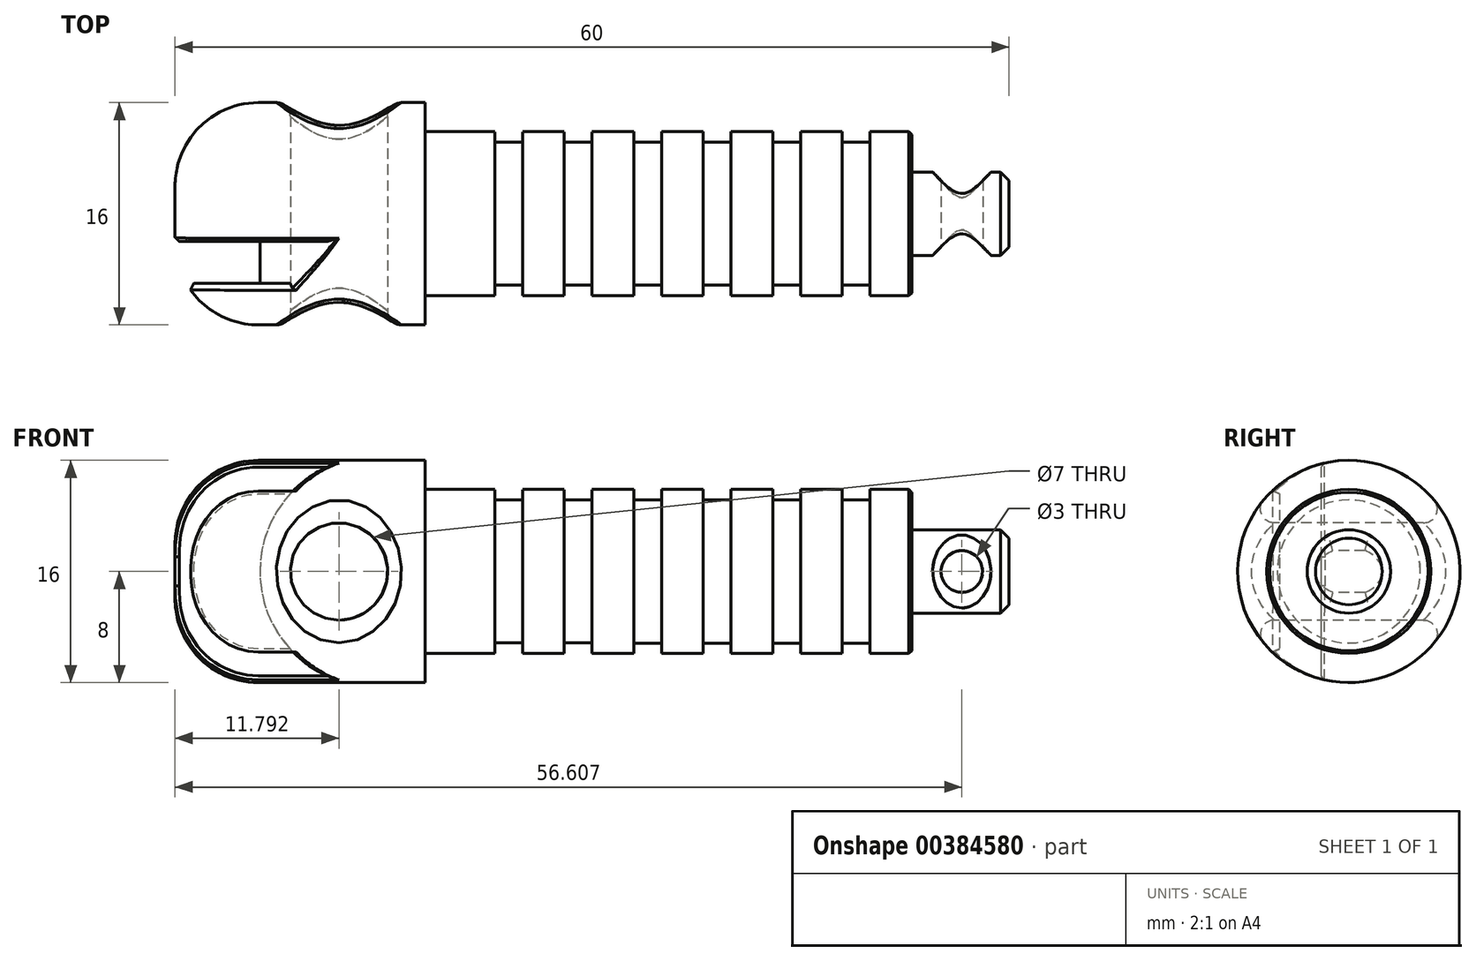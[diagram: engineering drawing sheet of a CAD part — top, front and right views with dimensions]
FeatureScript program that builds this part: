
annotation { "Feature Type Name" : "Feature", "Feature Type Description" : "" }
export const myFeature = defineFeature(function(context is Context, id is Id, definition is map)
    precondition{}
    {
        {
            var Q0;
            Q0=qCreatedBy(makeId("Right.planeOp"),FACE);
            var sketch = newSketch(context, id + "F0", { "sketchPlane" : qUnion([Q0])});
            skCircle(sketch, "E0", {"center": v(0, 0) * mm, "radius": 3 * mm});
            skSolve(sketch);
        }
        {
            var Q0;
            Q0=qSketchRegion(id+"F0",true);
            extrude(context, id + "F1", {"entities" : qUnion([Q0]), "depth" : 7 * mm});
        }
        {
            var Q0;
            Q0=makeQuery(id+"F1.opExtrude","CAP_FACE",FACE,{"disambiguationData":[OSD([sQuery(id+"F0.wireOp",EDGE,"E0")])],"isStart":true});
            var sketch = newSketch(context, id + "F2", { "sketchPlane" : qUnion([Q0])});
            skCircle(sketch, "E1", {"center": v(0, 0) * mm, "radius": 5.9 * mm});
            skSolve(sketch);
        }
        {
            var Q0;
            Q0=qSketchRegion(id+"F2",true);
            extrude(context, id + "F3", {"entities" : qUnion([Q0]), "operationType" : NewBodyOperationType.ADD, "depth" : 8 * mm});
        }
        {
            var Q0;
            Q0=makeQuery(id+"F3.opExtrude","CAP_FACE",FACE,{"disambiguationData":[OSD([sQuery(id+"F2.wireOp",EDGE,"E1")])],"isStart":false});
            var sketch = newSketch(context, id + "F4", { "sketchPlane" : qUnion([Q0])});
            skCircle(sketch, "E2", {"center": v(0, 0) * mm, "radius": 5.15 * mm});
            skSolve(sketch);
        }
        {
            var Q0;
            Q0=qSketchRegion(id+"F4",true);
            extrude(context, id + "F5", {"entities" : qUnion([Q0]), "operationType" : NewBodyOperationType.ADD, "depth" : 2 * mm});
        }
        {
            var Q0;
            Q0=makeQuery(id+"F5.opExtrude","CAP_FACE",FACE,{"disambiguationData":[OSD([sQuery(id+"F4.wireOp",EDGE,"E2")])],"isStart":false});
            var sketch = newSketch(context, id + "F6", { "sketchPlane" : qUnion([Q0])});
            skCircle(sketch, "E3", {"center": v(0, 0) * mm, "radius": 5.9 * mm});
            skSolve(sketch);
        }
        {
            var Q0;
            Q0=qSketchRegion(id+"F6",true);
            extrude(context, id + "F7", {"entities" : qUnion([Q0]), "operationType" : NewBodyOperationType.ADD, "depth" : 3 * mm});
        }
        {
            var Q0;
            Q0=makeQuery(id+"F7.opExtrude","CAP_FACE",FACE,{"disambiguationData":[OSD([sQuery(id+"F6.wireOp",EDGE,"E3")])],"isStart":false});
            var sketch = newSketch(context, id + "F8", { "sketchPlane" : qUnion([Q0])});
            skCircle(sketch, "E4", {"center": v(0, 0) * mm, "radius": 5.15 * mm});
            skSolve(sketch);
        }
        {
            var Q0;
            Q0=qSketchRegion(id+"F8",true);
            extrude(context, id + "F9", {"entities" : qUnion([Q0]), "operationType" : NewBodyOperationType.ADD, "depth" : 2 * mm});
        }
        {
            var Q0;
            Q0=makeQuery(id+"F9.opExtrude","CAP_FACE",FACE,{"disambiguationData":[OSD([sQuery(id+"F8.wireOp",EDGE,"E4")])],"isStart":false});
            var sketch = newSketch(context, id + "F10", { "sketchPlane" : qUnion([Q0])});
            skCircle(sketch, "E5", {"center": v(0, 0) * mm, "radius": 5.9 * mm});
            skSolve(sketch);
        }
        {
            var Q0;
            Q0=qSketchRegion(id+"F10",true);
            extrude(context, id + "F11", {"entities" : qUnion([Q0]), "operationType" : NewBodyOperationType.ADD, "depth" : 3 * mm});
        }
        {
            var Q0;
            Q0=makeQuery(id+"F11.opExtrude","CAP_FACE",FACE,{"disambiguationData":[OSD([sQuery(id+"F10.wireOp",EDGE,"E5")])],"isStart":false});
            var sketch = newSketch(context, id + "F12", { "sketchPlane" : qUnion([Q0])});
            skCircle(sketch, "E6", {"center": v(0, 0) * mm, "radius": 5.15 * mm});
            skSolve(sketch);
        }
        {
            var Q0;
            Q0=qSketchRegion(id+"F12",true);
            extrude(context, id + "F13", {"entities" : qUnion([Q0]), "operationType" : NewBodyOperationType.ADD, "depth" : 2 * mm});
        }
        {
            var Q0;
            Q0=makeQuery(id+"F13.opExtrude","CAP_FACE",FACE,{"disambiguationData":[OSD([sQuery(id+"F12.wireOp",EDGE,"E6")])],"isStart":false});
            var sketch = newSketch(context, id + "F14", { "sketchPlane" : qUnion([Q0])});
            skCircle(sketch, "E7", {"center": v(0, 0) * mm, "radius": 5.9 * mm});
            skSolve(sketch);
        }
        {
            var Q0;
            Q0=qSketchRegion(id+"F14",true);
            extrude(context, id + "F15", {"entities" : qUnion([Q0]), "operationType" : NewBodyOperationType.ADD, "depth" : 15 * mm});
        }
        {
            var Q0;
            Q0=makeQuery(id+"F15.opExtrude","CAP_FACE",FACE,{"disambiguationData":[OSD([sQuery(id+"F14.wireOp",EDGE,"E7")])],"isStart":false});
            var sketch = newSketch(context, id + "F16", { "sketchPlane" : qUnion([Q0])});
            skCircle(sketch, "E8", {"center": v(0, 0) * mm, "radius": 8 * mm});
            skSolve(sketch);
        }
        {
            var Q0;
            Q0=qSketchRegion(id+"F16",true);
            extrude(context, id + "F17", {"entities" : qUnion([Q0]), "operationType" : NewBodyOperationType.ADD, "depth" : 18 * mm});
        }
        {
            var Q0;
            Q0=makeQuery(id+"F3.opExtrude","CAP_EDGE",EDGE,{"disambiguationData":[OSD([sQuery(id+"F2.wireOp",EDGE,"E1")])],"isStart":true});
            chamfer(context, id + "F18", {"entities" : qUnion([Q0]), "width" : .2 * mm, "tangentPropagation" : true});
        }
        {
            var Q0;
            Q0=qCreatedBy(makeId("Front.planeOp"),FACE);
            var sketch = newSketch(context, id + "F19", { "sketchPlane" : qUnion([Q0])});
            skCircle(sketch, "E9", {"center": v(3.6, 0) * mm, "radius": 1.5 * mm});
            skSolve(sketch);
        }
        {
            var Q0;
            Q0=qSketchRegion(id+"F19",true);
            extrude(context, id + "F20", {"entities" : qUnion([Q0]), "operationType" : NewBodyOperationType.REMOVE, "endBound" : BoundingType.THROUGH_ALL, "oppositeDirection" : true, "depth" : 25 * mm, "hasSecondDirection" : true, "secondDirectionBound" : SecondDirectionBoundingType.THROUGH_ALL, "secondDirectionOppositeDirection" : false, "secondDirectionDepth" : 25 * mm});
        }
        {
            var Q0;
            Q0=makeQuery(id+"F20.boolean.opBoolean","INTERSECT",EDGE,{"disambiguationData":[OD(0.0)],"derivedFrom":[makeQuery(id+"F1.opExtrude","SWEPT_FACE",FACE,{"disambiguationData":[OSD([sQuery(id+"F0.wireOp",EDGE,"E0")])]}),makeQuery(id+"F20.opExtrude","SWEPT_FACE",FACE,{"disambiguationData":[OSD([sQuery(id+"F19.wireOp",EDGE,"E9")])]})]});
            var Q1;
            Q1=makeQuery(id+"F20.boolean.opBoolean","INTERSECT",EDGE,{"disambiguationData":[OD(1.0)],"derivedFrom":[makeQuery(id+"F1.opExtrude","SWEPT_FACE",FACE,{"disambiguationData":[OSD([sQuery(id+"F0.wireOp",EDGE,"E0")])]}),makeQuery(id+"F20.opExtrude","SWEPT_FACE",FACE,{"disambiguationData":[OSD([sQuery(id+"F19.wireOp",EDGE,"E9")])]})]});
            var Q2;
            Q2=makeQuery(id+"F1.opExtrude","CAP_EDGE",EDGE,{"disambiguationData":[OSD([sQuery(id+"F0.wireOp",EDGE,"E0")])],"isStart":false});
            chamfer(context, id + "F21", {"entities" : qUnion([Q0, Q1, Q2]), "width" : .6 * mm, "tangentPropagation" : true});
        }
        {
            var Q0;
            Q0=qCreatedBy(makeId("Front.planeOp"),FACE);
            var sketch = newSketch(context, id + "F22", { "sketchPlane" : qUnion([Q0])});
            skCircle(sketch, "E10", {"center": v(-126.5, 0) * mm, "radius": 4 * mm});
            skCircle(sketch, "E11", {"center": v(-41.2, 0) * mm, "radius": 3.5 * mm});
            skSolve(sketch);
        }
        {
            var Q0;
            Q0=qSketchRegion(id+"F22",true);
            extrude(context, id + "F23", {"entities" : qUnion([Q0]), "operationType" : NewBodyOperationType.REMOVE, "endBound" : BoundingType.THROUGH_ALL, "oppositeDirection" : true, "depth" : 25 * mm, "hasSecondDirection" : true, "secondDirectionBound" : SecondDirectionBoundingType.THROUGH_ALL, "secondDirectionOppositeDirection" : false, "secondDirectionDepth" : 25 * mm});
        }
        {
            var Q0;
            Q0=qCreatedBy(makeId("Front.planeOp"),FACE);
            var sketch = newSketch(context, id + "F24", { "sketchPlane" : qUnion([Q0])});
            skLineSegment(sketch, "E12", {"start": v(-23, 5.9) * mm, "end": v(-23, 3.5) * mm, "construction": true});
            skLineSegment(sketch, "E13.bottom", {"start": v(-23, 5.9) * mm, "end": v(-25, 5.9) * mm});
            skLineSegment(sketch, "E13.top", {"start": v(-23, 5.15) * mm, "end": v(-25, 5.15) * mm});
            skLineSegment(sketch, "E13.left", {"start": v(-23, 5.9) * mm, "end": v(-23, 5.15) * mm});
            skLineSegment(sketch, "E13.right", {"start": v(-25, 5.9) * mm, "end": v(-25, 5.15) * mm});
            skLineSegment(sketch, "E14.bottom", {"start": v(-28, 5.15) * mm, "end": v(-30, 5.15) * mm});
            skLineSegment(sketch, "E14.top", {"start": v(-28, 5.9) * mm, "end": v(-30, 5.9) * mm});
            skLineSegment(sketch, "E14.left", {"start": v(-28, 5.15) * mm, "end": v(-28, 5.9) * mm});
            skLineSegment(sketch, "E14.right", {"start": v(-30, 5.15) * mm, "end": v(-30, 5.9) * mm});
            skSolve(sketch);
        }
        {
            var Q0;
            Q0=qSketchRegion(id+"F24",true);
            var Q1;
            Q1=qConstructionFilter(qBodyType(qCreatedBy(id+"F24",EDGE),BodyType.WIRE),ConstructionObject.NO);
            var Q2;
            {var subQ0=sQuery(id+"F2.wireOp",EDGE,"E1");Q2=makeQuery(id+"F18.opChamfer","BLEND_EDGE",EDGE,{"blendedFrom":[makeQuery(id+"F3.opExtrude","CAP_EDGE",EDGE,{"disambiguationData":[OSD([subQ0])],"isStart":true}),makeQuery(id+"F3.opExtrude","SWEPT_FACE",FACE,{"disambiguationData":[OSD([subQ0])]})],"blendedInto":[makeQuery(id+"F3.opExtrude","SWEPT_FACE",FACE,{"disambiguationData":[OSD([subQ0])]})]});}
            revolve(context, id + "F25", {"operationType" : NewBodyOperationType.REMOVE, "entities" : qUnion([Q0]), "surfaceEntities" : qUnion([Q1]), "axis" : qUnion([Q2]), "revolveType" : RevolveType.FULL});
        }
        {
            var Q0;
            Q0=qCreatedBy(makeId("Front.planeOp"),FACE);
            var sketch = newSketch(context, id + "F26", { "sketchPlane" : qUnion([Q0])});
            skCircle(sketch, "E15", {"center": v(-38.67, 0) * mm, "radius": 8.23 * mm});
            skLineSegment(sketch, "E16", {"start": v(-38.89, 8.23) * mm, "end": v(-55.45, 8.23) * mm});
            skLineSegment(sketch, "E17", {"start": v(-55.45, 8.23) * mm, "end": v(-55.45, -8.39) * mm});
            skLineSegment(sketch, "E18", {"start": v(-55.45, -8.39) * mm, "end": v(-38.6, -8.23) * mm});
            skSolve(sketch);
        }
        {
            var Q0;
            {var subQ0=sQuery(id+"F26.wireOp",EDGE,"E16");Q0=makeQuery(id+"F26.imprint","IMPRINT",FACE,{"disambiguationData":[TD([[makeQuery(id+"F26.imprint","IMPRINT",EDGE,{"derivedFrom":subQ0}),1.0]])]});}
            extrude(context, id + "F27", {"entities" : qUnion([Q0]), "operationType" : NewBodyOperationType.REMOVE, "depth" : 5 * mm, "hasSecondDirection" : true, "secondDirectionOppositeDirection" : false, "secondDirectionDepth" : 2 * mm});
        }
        {
            var Q0;
            {var subQ0=sQuery(id+"F16.wireOp",EDGE,"E8");Q0=makeQuery(id+"F27.boolean.opBoolean","SPLIT",EDGE,{"disambiguationData":[TD([makeQuery(id+"F27.opExtrude","CAP_FACE",FACE,{"disambiguationData":[OSD([sQuery(id+"F26.wireOp",EDGE,"E15"),sQuery(id+"F26.wireOp",EDGE,"E16"),sQuery(id+"F26.wireOp",EDGE,"tU1BzypC-NC8o-H1pm-hXLC-StGrxM40IXlg"),sQuery(id+"F26.wireOp",EDGE,"Lf4QsQdu-0aue-FuZr-Vek4-Tb9GEt2DMBoj")])],"isStart":false})])],"derivedFrom":makeQuery(id+"F17.opExtrude","CAP_EDGE",EDGE,{"disambiguationData":[OSD([subQ0])],"isStart":false})});}
            var Q1;
            {var subQ0=sQuery(id+"F16.wireOp",EDGE,"E8");Q1=makeQuery(id+"F27.boolean.opBoolean","SPLIT",EDGE,{"disambiguationData":[TD([makeQuery(id+"F27.opExtrude","CAP_FACE",FACE,{"disambiguationData":[OSD([sQuery(id+"F26.wireOp",EDGE,"E15"),sQuery(id+"F26.wireOp",EDGE,"E16"),sQuery(id+"F26.wireOp",EDGE,"tU1BzypC-NC8o-H1pm-hXLC-StGrxM40IXlg"),sQuery(id+"F26.wireOp",EDGE,"Lf4QsQdu-0aue-FuZr-Vek4-Tb9GEt2DMBoj")])],"isStart":true})])],"derivedFrom":makeQuery(id+"F17.opExtrude","CAP_EDGE",EDGE,{"disambiguationData":[OSD([subQ0])],"isStart":false})});}
            fillet(context, id + "F28", {"entities" : qUnion([Q0, Q1]), "radius" : 6 * mm, "tangentPropagation" : true, "allowEdgeOverflow" : false});
        }
        {
            var Q0;
            {var subQ0=makeQuery(id+"F27.opExtrude","CAP_FACE",FACE,{"disambiguationData":[OSD([sQuery(id+"F26.wireOp",EDGE,"E15"),sQuery(id+"F26.wireOp",EDGE,"E16"),sQuery(id+"F26.wireOp",EDGE,"tU1BzypC-NC8o-H1pm-hXLC-StGrxM40IXlg"),sQuery(id+"F26.wireOp",EDGE,"Lf4QsQdu-0aue-FuZr-Vek4-Tb9GEt2DMBoj")])],"isStart":true});var subQ1=sQuery(id+"F16.wireOp",EDGE,"E8");Q0=makeQuery(id+"F28.opFillet","BLEND_EDGE",EDGE,{"disambiguationData":[OD(1.0)],"blendedFrom":[makeQuery(id+"F27.boolean.opBoolean","SPLIT",EDGE,{"disambiguationData":[TD([subQ0])],"derivedFrom":makeQuery(id+"F17.opExtrude","CAP_EDGE",EDGE,{"disambiguationData":[OSD([subQ1])],"isStart":false})}),makeQuery(id+"F27.boolean.opBoolean","COPY",FACE,{"derivedFrom":subQ0})],"blendedInto":[makeQuery(id+"F27.boolean.opBoolean","COPY",FACE,{"derivedFrom":subQ0})]});}
            var Q1;
            {var subQ0=makeQuery(id+"F27.opExtrude","CAP_FACE",FACE,{"disambiguationData":[OSD([sQuery(id+"F26.wireOp",EDGE,"E15"),sQuery(id+"F26.wireOp",EDGE,"E16"),sQuery(id+"F26.wireOp",EDGE,"tU1BzypC-NC8o-H1pm-hXLC-StGrxM40IXlg"),sQuery(id+"F26.wireOp",EDGE,"Lf4QsQdu-0aue-FuZr-Vek4-Tb9GEt2DMBoj")])],"isStart":true});var subQ1=sQuery(id+"F16.wireOp",EDGE,"E8");Q1=makeQuery(id+"F28.opFillet","BLEND_EDGE",EDGE,{"disambiguationData":[OD(0.0)],"blendedFrom":[makeQuery(id+"F27.boolean.opBoolean","SPLIT",EDGE,{"disambiguationData":[TD([subQ0])],"derivedFrom":makeQuery(id+"F17.opExtrude","CAP_EDGE",EDGE,{"disambiguationData":[OSD([subQ1])],"isStart":false})}),makeQuery(id+"F27.boolean.opBoolean","COPY",FACE,{"derivedFrom":subQ0})],"blendedInto":[makeQuery(id+"F27.boolean.opBoolean","COPY",FACE,{"derivedFrom":subQ0})]});}
            var Q2;
            {var subQ0=makeQuery(id+"F27.opExtrude","CAP_FACE",FACE,{"disambiguationData":[OSD([sQuery(id+"F26.wireOp",EDGE,"E15"),sQuery(id+"F26.wireOp",EDGE,"E16"),sQuery(id+"F26.wireOp",EDGE,"tU1BzypC-NC8o-H1pm-hXLC-StGrxM40IXlg"),sQuery(id+"F26.wireOp",EDGE,"Lf4QsQdu-0aue-FuZr-Vek4-Tb9GEt2DMBoj")])],"isStart":false});var subQ1=sQuery(id+"F16.wireOp",EDGE,"E8");Q2=makeQuery(id+"F28.opFillet","BLEND_EDGE",EDGE,{"blendedFrom":[makeQuery(id+"F27.boolean.opBoolean","SPLIT",EDGE,{"disambiguationData":[TD([subQ0])],"derivedFrom":makeQuery(id+"F17.opExtrude","CAP_EDGE",EDGE,{"disambiguationData":[OSD([subQ1])],"isStart":false})}),makeQuery(id+"F27.boolean.opBoolean","COPY",FACE,{"derivedFrom":subQ0})],"blendedInto":[makeQuery(id+"F27.boolean.opBoolean","COPY",FACE,{"derivedFrom":subQ0})]});}
            var Q3;
            Q3=makeQuery(id+"F27.boolean.opBoolean","INTERSECT",EDGE,{"disambiguationData":[OD(0.0)],"derivedFrom":[makeQuery(id+"F17.opExtrude","SWEPT_FACE",FACE,{"disambiguationData":[OSD([sQuery(id+"F16.wireOp",EDGE,"E8")])]}),makeQuery(id+"F27.opExtrude","CAP_FACE",FACE,{"disambiguationData":[OSD([sQuery(id+"F26.wireOp",EDGE,"E15"),sQuery(id+"F26.wireOp",EDGE,"E16"),sQuery(id+"F26.wireOp",EDGE,"tU1BzypC-NC8o-H1pm-hXLC-StGrxM40IXlg"),sQuery(id+"F26.wireOp",EDGE,"Lf4QsQdu-0aue-FuZr-Vek4-Tb9GEt2DMBoj")])],"isStart":true})]});
            var Q4;
            Q4=makeQuery(id+"F27.boolean.opBoolean","INTERSECT",EDGE,{"disambiguationData":[OD(0.0)],"derivedFrom":[makeQuery(id+"F17.opExtrude","SWEPT_FACE",FACE,{"disambiguationData":[OSD([sQuery(id+"F16.wireOp",EDGE,"E8")])]}),makeQuery(id+"F27.opExtrude","SWEPT_FACE",FACE,{"disambiguationData":[OSD([sQuery(id+"F26.wireOp",EDGE,"E15")])]})]});
            var Q5;
            Q5=makeQuery(id+"F27.boolean.opBoolean","INTERSECT",EDGE,{"disambiguationData":[OD(0.0)],"derivedFrom":[makeQuery(id+"F17.opExtrude","SWEPT_FACE",FACE,{"disambiguationData":[OSD([sQuery(id+"F16.wireOp",EDGE,"E8")])]}),makeQuery(id+"F27.opExtrude","CAP_FACE",FACE,{"disambiguationData":[OSD([sQuery(id+"F26.wireOp",EDGE,"E15"),sQuery(id+"F26.wireOp",EDGE,"E16"),sQuery(id+"F26.wireOp",EDGE,"tU1BzypC-NC8o-H1pm-hXLC-StGrxM40IXlg"),sQuery(id+"F26.wireOp",EDGE,"Lf4QsQdu-0aue-FuZr-Vek4-Tb9GEt2DMBoj")])],"isStart":false})]});
            var Q6;
            Q6=makeQuery(id+"F27.boolean.opBoolean","INTERSECT",EDGE,{"disambiguationData":[OD(1.0)],"derivedFrom":[makeQuery(id+"F17.opExtrude","SWEPT_FACE",FACE,{"disambiguationData":[OSD([sQuery(id+"F16.wireOp",EDGE,"E8")])]}),makeQuery(id+"F27.opExtrude","CAP_FACE",FACE,{"disambiguationData":[OSD([sQuery(id+"F26.wireOp",EDGE,"E15"),sQuery(id+"F26.wireOp",EDGE,"E16"),sQuery(id+"F26.wireOp",EDGE,"tU1BzypC-NC8o-H1pm-hXLC-StGrxM40IXlg"),sQuery(id+"F26.wireOp",EDGE,"Lf4QsQdu-0aue-FuZr-Vek4-Tb9GEt2DMBoj")])],"isStart":false})]});
            var Q7;
            Q7=makeQuery(id+"F27.boolean.opBoolean","INTERSECT",EDGE,{"disambiguationData":[OD(1.0)],"derivedFrom":[makeQuery(id+"F17.opExtrude","SWEPT_FACE",FACE,{"disambiguationData":[OSD([sQuery(id+"F16.wireOp",EDGE,"E8")])]}),makeQuery(id+"F27.opExtrude","SWEPT_FACE",FACE,{"disambiguationData":[OSD([sQuery(id+"F26.wireOp",EDGE,"E15")])]})]});
            var Q8;
            Q8=makeQuery(id+"F27.boolean.opBoolean","INTERSECT",EDGE,{"disambiguationData":[OD(1.0)],"derivedFrom":[makeQuery(id+"F17.opExtrude","SWEPT_FACE",FACE,{"disambiguationData":[OSD([sQuery(id+"F16.wireOp",EDGE,"E8")])]}),makeQuery(id+"F27.opExtrude","CAP_FACE",FACE,{"disambiguationData":[OSD([sQuery(id+"F26.wireOp",EDGE,"E15"),sQuery(id+"F26.wireOp",EDGE,"E16"),sQuery(id+"F26.wireOp",EDGE,"tU1BzypC-NC8o-H1pm-hXLC-StGrxM40IXlg"),sQuery(id+"F26.wireOp",EDGE,"Lf4QsQdu-0aue-FuZr-Vek4-Tb9GEt2DMBoj")])],"isStart":true})]});
            chamfer(context, id + "F29", {"entities" : qUnion([Q0, Q1, Q2, Q3, Q4, Q5, Q6, Q7, Q8]), "width" : .3 * mm, "tangentPropagation" : true});
        }
        {
            var Q0;
            Q0=qCreatedBy(makeId("Front.planeOp"),FACE);
            var sketch = newSketch(context, id + "F30", { "sketchPlane" : qUnion([Q0])});
            skLineSegment(sketch, "E19", {"start": v(-7.42, 5.15) * mm, "end": v(1.16, 5.15) * mm, "construction": true});
            skLineSegment(sketch, "E20.bottom", {"start": v(-5, 5.15) * mm, "end": v(-3, 5.15) * mm, "construction": true});
            skLineSegment(sketch, "E20.top", {"start": v(-5, 6.32) * mm, "end": v(-3, 6.32) * mm, "construction": true});
            skLineSegment(sketch, "E20.left", {"start": v(-5, 5.15) * mm, "end": v(-5, 6.32) * mm, "construction": true});
            skLineSegment(sketch, "E20.right", {"start": v(-3, 5.15) * mm, "end": v(-3, 6.32) * mm, "construction": true});
            skLineSegment(sketch, "E21.bottom", {"start": v(-5, 5.15) * mm, "end": v(-3, 5.15) * mm});
            skLineSegment(sketch, "E21.top", {"start": v(-5, 6.32) * mm, "end": v(-3, 6.32) * mm});
            skLineSegment(sketch, "E21.left", {"start": v(-5, 5.15) * mm, "end": v(-5, 6.32) * mm});
            skLineSegment(sketch, "E21.right", {"start": v(-3, 5.15) * mm, "end": v(-3, 6.32) * mm});
            skSolve(sketch);
        }
        {
            var Q0;
            Q0 = qSketchRegion(id + "F30", true);
            var Q1;
            {var subQ0=sQuery(id+"F2.wireOp",EDGE,"E1");Q1=makeQuery(id+"F18.opChamfer","BLEND_EDGE",EDGE,{"blendedFrom":[makeQuery(id+"F3.opExtrude","CAP_EDGE",EDGE,{"disambiguationData":[OSD([subQ0])],"isStart":true}),makeQuery(id+"F3.opExtrude","CAP_FACE",FACE,{"disambiguationData":[OSD([subQ0])],"isStart":true})],"blendedInto":[makeQuery(id+"F3.opExtrude","CAP_FACE",FACE,{"disambiguationData":[OSD([subQ0])],"isStart":true})]});}
            revolve(context, id + "F31", {"operationType" : NewBodyOperationType.REMOVE, "entities" : qUnion([Q0]), "axis" : qUnion([Q1]), "revolveType" : RevolveType.FULL, "oppositeDirection" : true});
        }
        {
            var Q0;
            Q0=makeQuery(id+"F23.boolean.opBoolean","INTERSECT",EDGE,{"disambiguationData":[OD(0.0)],"derivedFrom":[makeQuery(id+"F17.opExtrude","SWEPT_FACE",FACE,{"disambiguationData":[OSD([sQuery(id+"F16.wireOp",EDGE,"E8")])]}),makeQuery(id+"F23.opExtrude","SWEPT_FACE",FACE,{"disambiguationData":[OSD([sQuery(id+"F22.wireOp",EDGE,"E11")])]})]});
            var Q1;
            Q1=makeQuery(id+"F23.boolean.opBoolean","INTERSECT",EDGE,{"disambiguationData":[OD(1.0)],"derivedFrom":[makeQuery(id+"F17.opExtrude","SWEPT_FACE",FACE,{"disambiguationData":[OSD([sQuery(id+"F16.wireOp",EDGE,"E8")])]}),makeQuery(id+"F23.opExtrude","SWEPT_FACE",FACE,{"disambiguationData":[OSD([sQuery(id+"F22.wireOp",EDGE,"E11")])]})]});
            fillet(context, id + "F32", {"entities" : qUnion([Q0, Q1]), "radius" : 1 * mm, "tangentPropagation" : true, "allowEdgeOverflow" : false});
        }
    });
